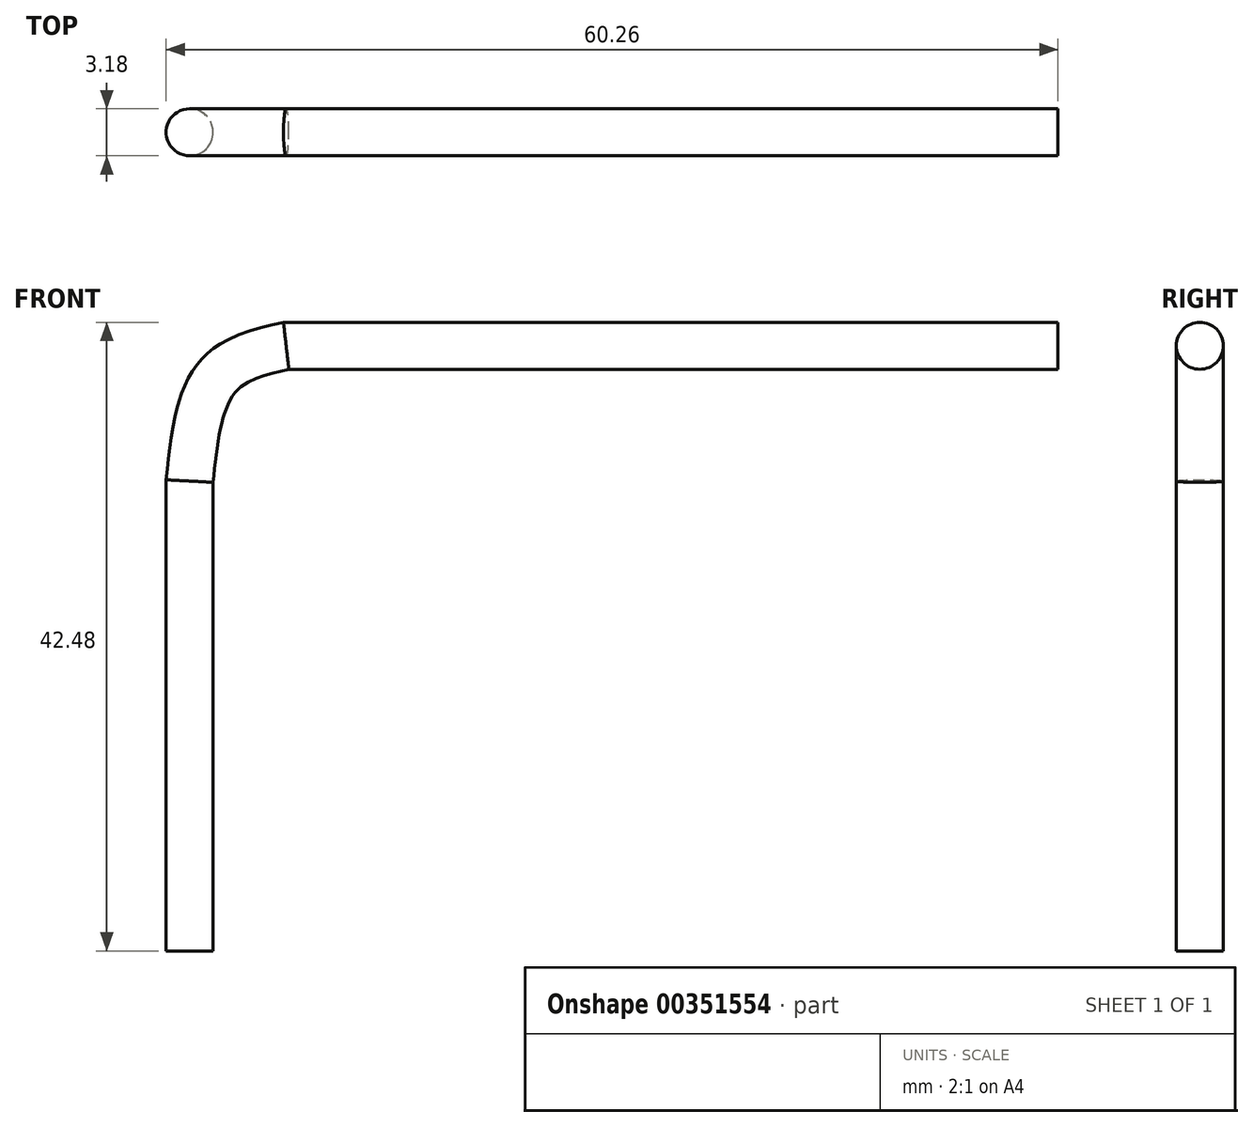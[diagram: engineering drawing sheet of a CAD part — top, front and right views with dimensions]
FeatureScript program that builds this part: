
annotation { "Feature Type Name" : "Feature", "Feature Type Description" : "" }
export const myFeature = defineFeature(function(context is Context, id is Id, definition is map)
    precondition{}
    {
        {
            var Q0;
            Q0=qCreatedBy(makeId("Top.planeOp"),FACE);
            var sketch = newSketch(context, id + "F0", { "sketchPlane" : qUnion([Q0])});
            skCircle(sketch, "E0", {"center": v(0, 0) * mm, "radius": 1.59 * mm});
            skSolve(sketch);
        }
        {
            var Q0;
            Q0=qCreatedBy(makeId("Front.planeOp"),FACE);
            var sketch = newSketch(context, id + "F1", { "sketchPlane" : qUnion([Q0])});
            skLineSegment(sketch, "E1", {"start": v(0, 0) * mm, "end": v(0, 31.75) * mm});
            skLineSegment(sketch, "E2", {"start": v(0, 31.75) * mm, "end": v(0, 40.9) * mm, "construction": true});
            skLineSegment(sketch, "E3", {"start": v(0, 40.9) * mm, "end": v(58.67, 40.9) * mm, "construction": true});
            skFitSpline(sketch, "E4", {"points": [v(0, 31.75) * mm, v(1.87, 38.8) * mm, v(6.52, 40.9) * mm], "startDerivative": vector(1.6, 15.2) * mm, "endDerivative": vector(11.75, 2.72) * mm});
            skLineSegment(sketch, "E5", {"start": v(6.52, 40.9) * mm, "end": v(58.67, 40.9) * mm});
            skSolve(sketch);
        }
        {
            var Q0;
            Q0 = qSketchRegion(id + "F0", true);
            var Q1;
            Q1 = qConstructionFilter(qBodyType(qCreatedBy(id + "F1" ,EDGE), BodyType.WIRE), ConstructionObject.NO);
            sweep(context, id + "F2", {"profiles" : qUnion([Q0]), "path" : qUnion([Q1])});
        }
    });
